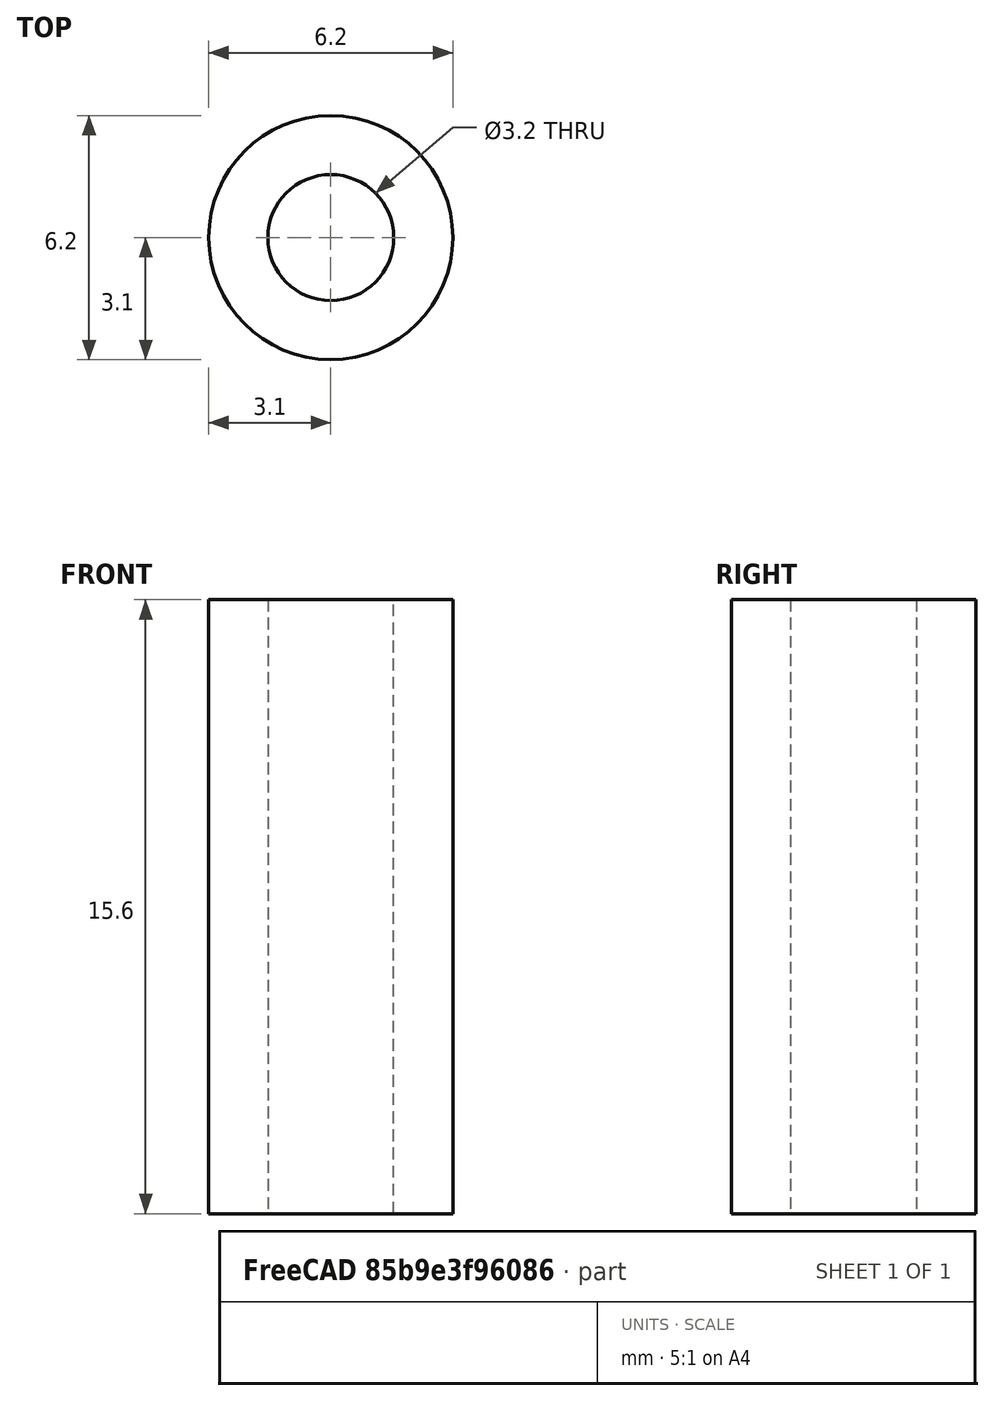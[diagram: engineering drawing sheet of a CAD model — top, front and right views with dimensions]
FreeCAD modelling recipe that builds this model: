
FCSTD DOCUMENT  (FreeCAD 0.21R33771 (Git))
Label: 6D2-3F2-15L6
License: All rights reserved
LicenseURL: http://en.wikipedia.org/wiki/All_rights_reserved
objects: Sketcher::SketchObject×1, PartDesign::Pad×1, PartDesign::Body×1
note: 4 computed .brp shape members not serialized (recipe doc carries the construction recipe); baked Part::Feature solids carry a one-line shape summary decoded from their .brp

FEATURE [Sketcher::SketchObject] Sketch
  FullyConstrained = true
  MapMode = 5
  Support = -> [XY_Plane]
  sketch-geometry (4):
    g0: Circle CenterX=0 CenterY=0 CenterZ=0 NormalX=0 NormalY=0 NormalZ=1 AngleXU=0 Radius=3.1
    g1: Circle CenterX=0 CenterY=0 CenterZ=0 NormalX=0 NormalY=0 NormalZ=1 AngleXU=0 Radius=1.6
    g2: GeomPoint X=3.1 Y=0 Z=0
    g3: GeomPoint X=1.6 Y=0 Z=0
  constraints (9):
    c: Coincident(g0,g-1)
    c: Coincident(g1,g0)
    c: Radius(g1) = 1.6
    c: PointOnObject(g3,g1)
    c: PointOnObject(g3,g-1)
    c: PointOnObject(g2,g0)
    c: PointOnObject(g2,g-1)
    c: DistanceX(g3,g2) = 1.5
    c: Radius(g0) = 3.1
FEATURE [PartDesign::Pad] Pad
  Direction = (0,0,1)
  Length = 15.6
  Length2 = 10
  Profile = -> Sketch
  ReferenceAxis = -> Sketch [N_Axis]
  Type = 0
FEATURE [PartDesign::Body] Body
  Group = -> [Sketch,Pad]
  Origin = -> Origin
  Tip = -> Pad
